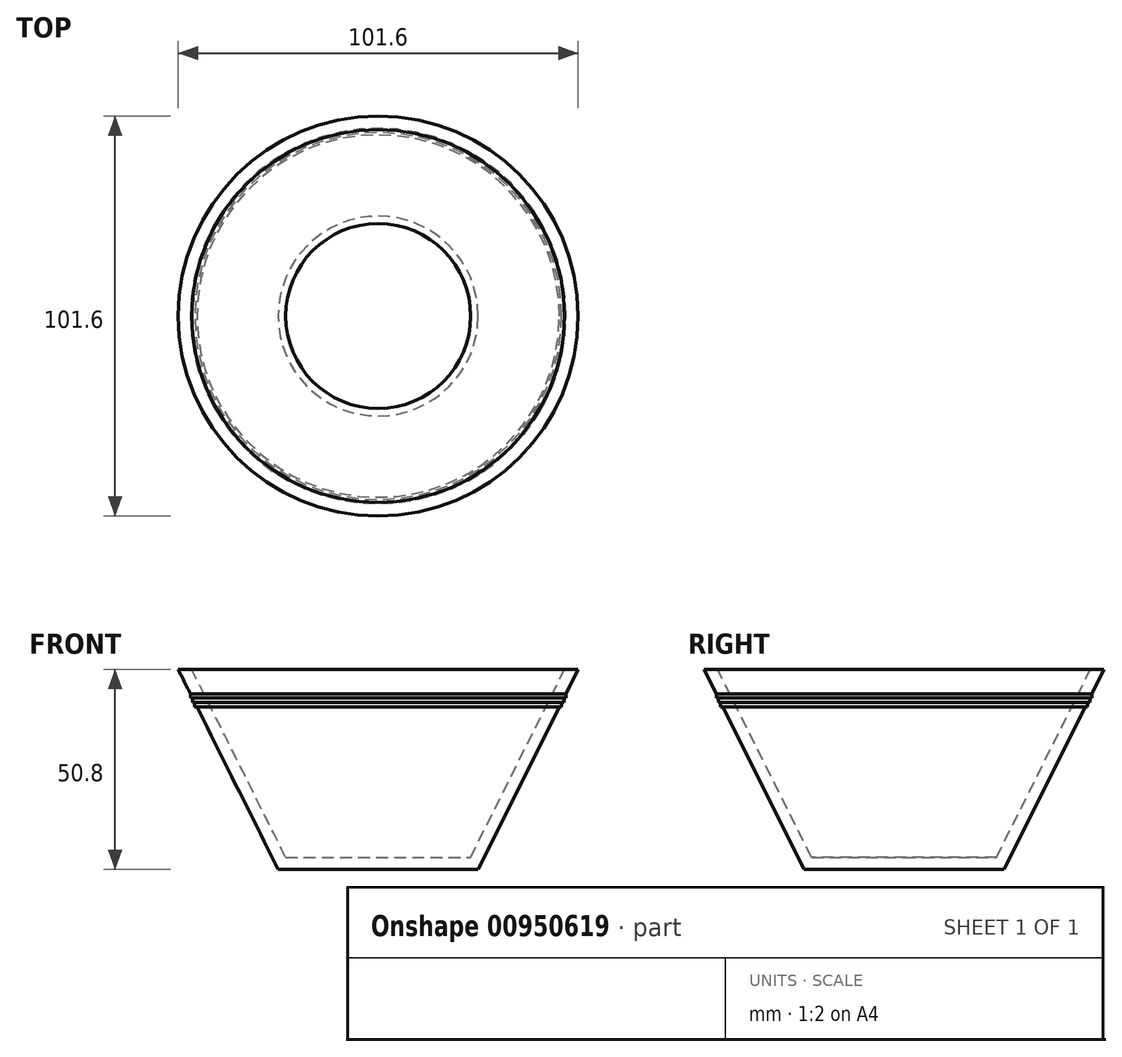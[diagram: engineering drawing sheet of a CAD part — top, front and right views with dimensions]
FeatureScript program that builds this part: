
annotation { "Feature Type Name" : "Feature", "Feature Type Description" : "" }
export const myFeature = defineFeature(function(context is Context, id is Id, definition is map)
    precondition{}
    {
        {
            var Q0;
            Q0=qCreatedBy(makeId("Front.planeOp"),FACE);
            var sketch = newSketch(context, id + "F0", { "sketchPlane" : qUnion([Q0])});
            skLineSegment(sketch, "E0", {"start": v(0, 0) * mm, "end": v(0, 50.8) * mm, "construction": true});
            skLineSegment(sketch, "E1", {"start": v(0, 0) * mm, "end": v(25.4, 0) * mm});
            skLineSegment(sketch, "E2", {"start": v(25.4, 0) * mm, "end": v(50.8, 50.8) * mm});
            skLineSegment(sketch, "E3.0", {"start": v(23.5, 3.07) * mm, "end": v(47.36, 50.8) * mm});
            skLineSegment(sketch, "E3.1", {"start": v(0, 3.07) * mm, "end": v(23.5, 3.07) * mm});
            skLineSegment(sketch, "E4", {"start": v(0, 3.07) * mm, "end": v(0, 0) * mm});
            skLineSegment(sketch, "E5", {"start": v(47.36, 50.8) * mm, "end": v(50.8, 50.8) * mm});
            skLineSegment(sketch, "E6", {"start": v(47.69, 44.57) * mm, "end": v(47.69, 43.58) * mm});
            skLineSegment(sketch, "E7", {"start": v(47.69, 43.58) * mm, "end": v(47.2, 43.58) * mm});
            skLineSegment(sketch, "E8", {"start": v(47.2, 43.58) * mm, "end": v(47.2, 42.43) * mm});
            skLineSegment(sketch, "E9", {"start": v(47.2, 42.43) * mm, "end": v(46.61, 42.43) * mm});
            skLineSegment(sketch, "E10", {"start": v(46.61, 42.43) * mm, "end": v(46.61, 41.27) * mm});
            skLineSegment(sketch, "E11", {"start": v(46.61, 41.27) * mm, "end": v(46.04, 41.27) * mm});
            skSolve(sketch);
        }
        {
            var Q0;
            Q0=makeQuery(id+"F0.imprint","IMPRINT",FACE,{"disambiguationData":[TD([[makeQuery(id+"F0.imprint","IMPRINT",EDGE,{"derivedFrom":sQuery(id+"F0.wireOp",EDGE,"E1")}),1.0]])]});
            var Q1;
            {var subQ0=sQuery(id+"F0.wireOp",EDGE,"E8");Q1=makeQuery(id+"F0.imprint","IMPRINT",FACE,{"disambiguationData":[TD([[makeQuery(id+"F0.imprint","IMPRINT",EDGE,{"derivedFrom":subQ0}),-1.0]])]});}
            var Q2;
            {var subQ0=sQuery(id+"F0.wireOp",EDGE,"E6");Q2=makeQuery(id+"F0.imprint","IMPRINT",FACE,{"disambiguationData":[TD([[makeQuery(id+"F0.imprint","IMPRINT",EDGE,{"derivedFrom":subQ0}),-1.0]])]});}
            var Q3;
            {var subQ0=sQuery(id+"F0.wireOp",EDGE,"E10");Q3=makeQuery(id+"F0.imprint","IMPRINT",FACE,{"disambiguationData":[TD([[makeQuery(id+"F0.imprint","IMPRINT",EDGE,{"derivedFrom":subQ0}),-1.0]])]});}
            var Q4;
            Q4=sQuery(id+"F0.wireOp",EDGE,"E0");
            revolve(context, id + "F1", {"surfaceOperationType" : NewSurfaceOperationType.NEW, "entities" : qUnion([Q0, Q1, Q2, Q3]), "axis" : qUnion([Q4]), "revolveType" : RevolveType.FULL});
        }
    });
